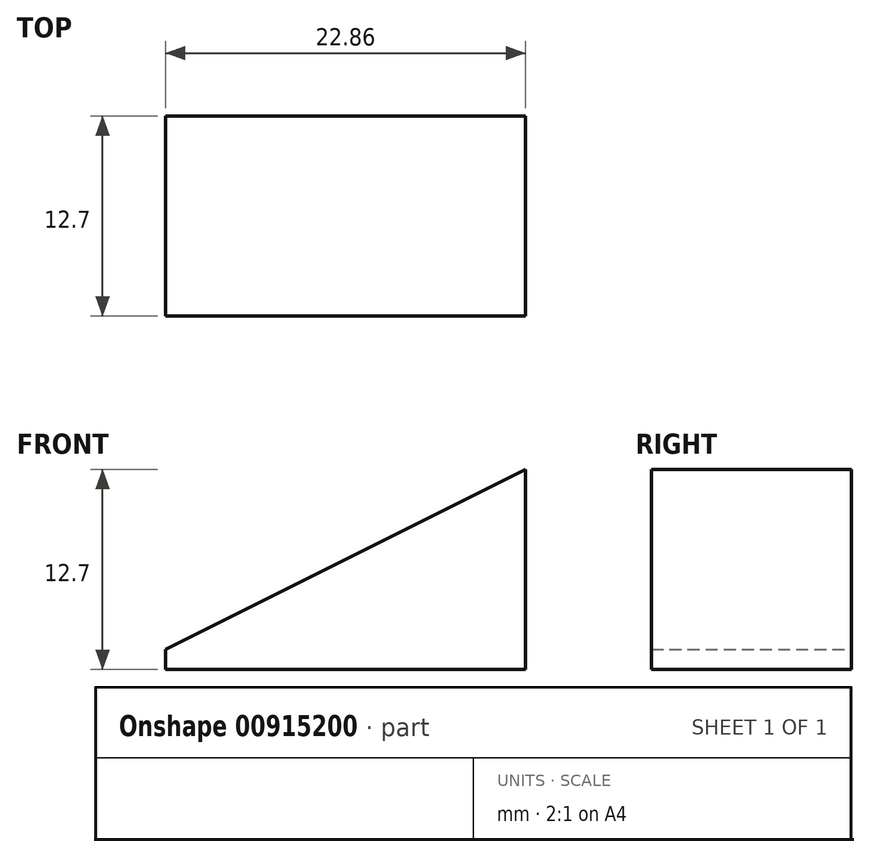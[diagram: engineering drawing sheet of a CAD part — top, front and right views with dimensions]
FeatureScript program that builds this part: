
annotation { "Feature Type Name" : "Feature", "Feature Type Description" : "" }
export const myFeature = defineFeature(function(context is Context, id is Id, definition is map)
    precondition{}
    {
        {
            var Q0;
            Q0=qCreatedBy(makeId("Front.planeOp"),FACE);
            var sketch = newSketch(context, id + "F0", { "sketchPlane" : qUnion([Q0])});
            skLineSegment(sketch, "E0", {"start": v(-11.3, 0) * mm, "end": v(11.55, 0) * mm});
            skLineSegment(sketch, "E1", {"start": v(11.55, 0) * mm, "end": v(11.55, 12.7) * mm});
            skLineSegment(sketch, "E2", {"start": v(-11.3, 0) * mm, "end": v(-11.3, 1.27) * mm});
            skLineSegment(sketch, "E3", {"start": v(-11.3, 1.27) * mm, "end": v(11.55, 12.7) * mm});
            skSolve(sketch);
        }
        {
            var Q0;
            Q0=makeQuery(id+"F0.imprint","IMPRINT",FACE,{"disambiguationData":[TD([[makeQuery(id+"F0.imprint","IMPRINT",EDGE,{"derivedFrom":sQuery(id+"F0.wireOp",EDGE,"E0")}),1.0]])]});
            extrude(context, id + "F1", {"entities" : qUnion([Q0]), "depth" : 12.7 * mm, "offsetDistance" : 25.4 * mm});
        }
    });
